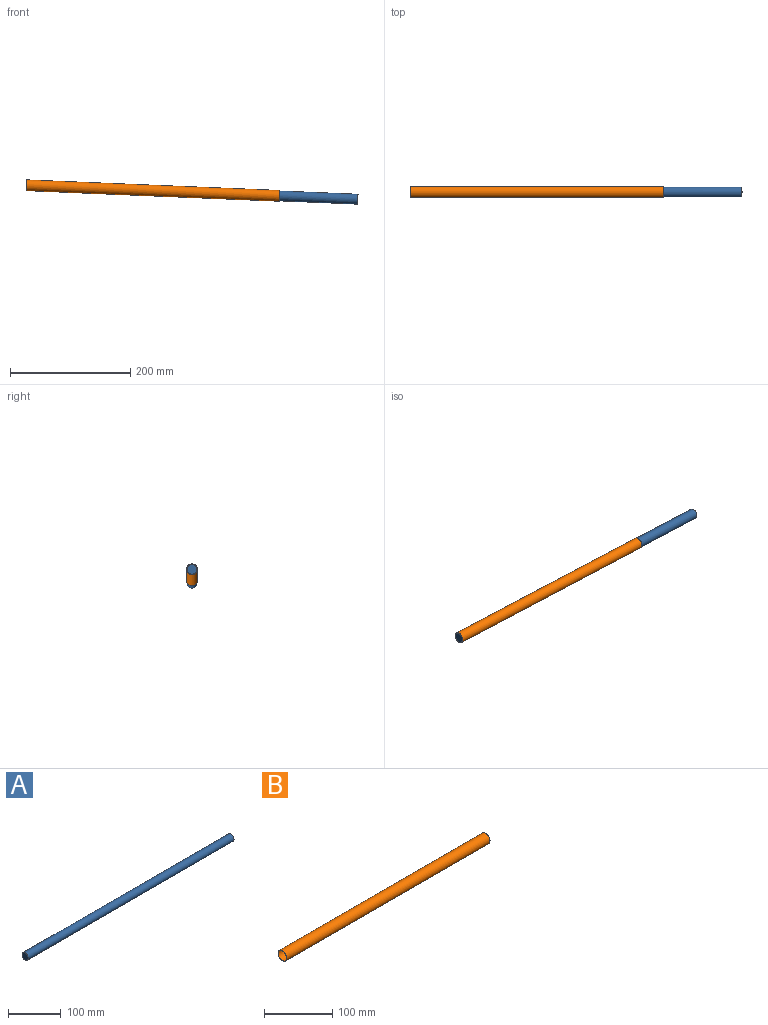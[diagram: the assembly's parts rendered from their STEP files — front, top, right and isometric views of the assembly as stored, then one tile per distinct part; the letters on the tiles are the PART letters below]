
ASSEMBLY  parts=2 mates=1
PART A: 3 faces, bbox 552.3x16.5x16.5 mm
  f0: cylinder r=8.26mm len=552.34mm, axis (-1,0,0), area 28648.7mm2, adj f1,f2
  f1: plane 16.51x16.51mm, normal (1,0,0), area 214.1mm2, adj f0
  f2: plane 16.51x16.51mm, normal (-1,0,0), area 214.1mm2, adj f0
PART B: 4 faces, bbox 421.9x18.2x18.2 mm
  f0: cylinder r=9.08mm len=421.89mm, axis (-1,0,0), area 24073.7mm2, adj f1,f2
  f1: plane 18.16x18.16mm, normal (1,0,0), area 10.8mm2, adj f0,f3
  f2: plane 18.16x18.16mm, normal (-1,0,0), area 10.8mm2, adj f0,f3
  f3: cylinder r=8.89mm len=421.89mm, axis (-1,0,0), area 23565.8mm2, adj f1,f2
PLACE A rot(axis=(0,1,0),2.4deg) t=(84.26,-87.99,13.39)mm
PLACE B rot(axis=(0,-1,0),177.6deg) t=(505.79,-87.99,-4.21)mm
MATE fastened A.f0 <-> B.f3  axis (-1,0,0.04) through (84.26,-87.99,13.39)mm
